# Revit family: Expansion Bolts-Side
name_source: partatom
category: Detail Items
revit_build: Autodesk Revit Architecture 2012 (Build: 20110210_1515)
units: mm (PartAtom-declared; Revit-internal decimal feet)

## types (6) — shared parameters

## per-type parameters (varying)
| type | D | D1 | D2 | D3 | F3 | F4 | H | H1 | Keynote | L1 | L2 | WH | WW | WW/2 |
| 3/8" | 0.375" | 0.047" | 0.094" | 0.141" | 0.176" | 0.352" | 0.234" | 0.188" | 05 05 23.G1 | 1.828" | 0.609" | 0.023" | 0.633" | 0.317" |
| 1/2" | 0.500" | 0.063" | 0.126" | 0.189" | 0.235" | 0.469" | 0.313" | 0.250" | 05 05 23.G2 | 2.438" | 0.813" | 0.031" | 0.844" | 0.422" |
| 5/8" | 0.625" | 0.078" | 0.156" | 0.234" | 0.293" | 0.586" | 0.391" | 0.313" | 05 05 23.G3 | 3.047" | 1.016" | 0.039" | 1.055" | 0.528" |
| 3/4" | 0.750" | 0.094" | 0.188" | 0.282" | 0.352" | 0.704" | 0.477" | 0.383" | 05 05 23.G4 | 3.656" | 1.219" | 0.047" | 1.266" | 0.633" |
| 7/8" | 0.875" | 0.109" | 0.218" | 0.327" | 0.410" | 0.821" | 0.547" | 0.438" | 05 05 23.G5 | 4.266" | 1.422" | 0.055" | 1.477" | 0.739" |
| 1" | 1.000" | 0.125" | 0.250" | 0.375" | 0.469" | 0.938" | 0.625" | 0.500" | 05 05 23.G6 | 4.875" | 1.625" | 0.063" | 1.688" | 0.844" |

## geometry (parser evidence)
native form markers: Sweep x1
no freeform markers — native parametric forms only
